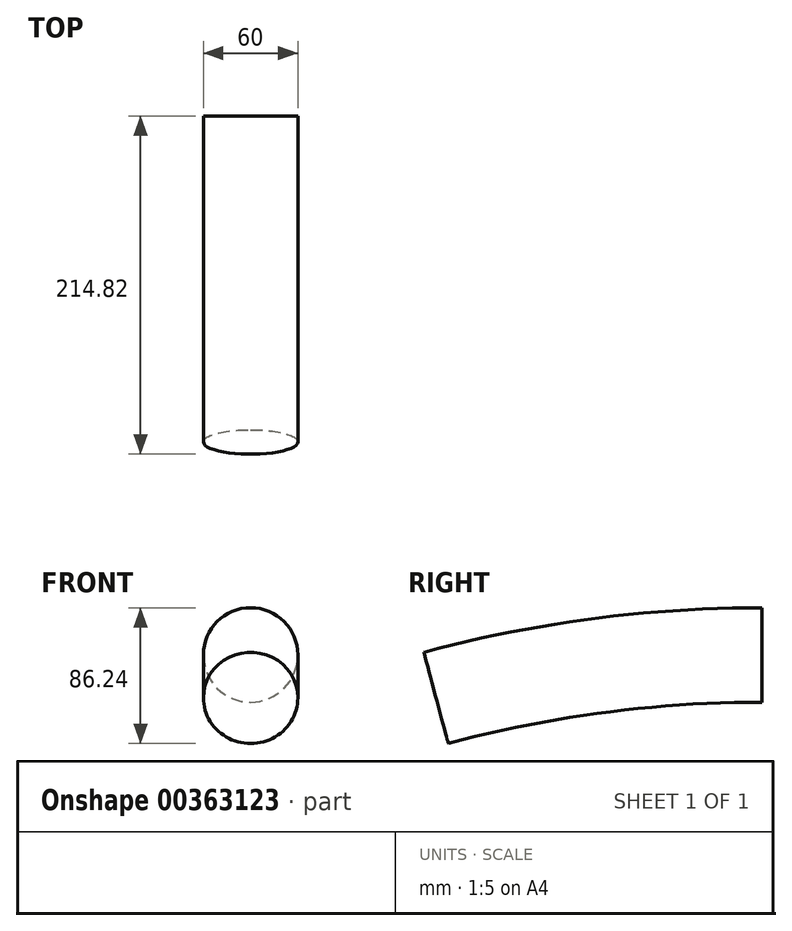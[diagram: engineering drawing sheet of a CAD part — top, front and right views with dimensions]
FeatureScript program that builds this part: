
annotation { "Feature Type Name" : "Feature", "Feature Type Description" : "" }
export const myFeature = defineFeature(function(context is Context, id is Id, definition is map)
    precondition{}
    {
        {
            var Q0;
            Q0=qCreatedBy(makeId("Front.planeOp"),FACE);
            var sketch = newSketch(context, id + "F0", { "sketchPlane" : qUnion([Q0])});
            skCircle(sketch, "E0", {"center": v(0, 0) * mm, "radius": 30 * mm});
            skLineSegment(sketch, "E1", {"start": v(-105.94, -800) * mm, "end": v(170.5, -800) * mm});
            skSolve(sketch);
        }
        {
            var Q0;
            Q0 = qSketchRegion(id + "F0", true);
            var Q1;
            Q1=sQuery(id+"F0.wireOp",EDGE,"E1");
            revolve(context, id + "F1", {"entities" : qUnion([Q0]), "axis" : qUnion([Q1]), "revolveType" : RevolveType.ONE_DIRECTION, "angle" : 15 * degree});
        }
    });
